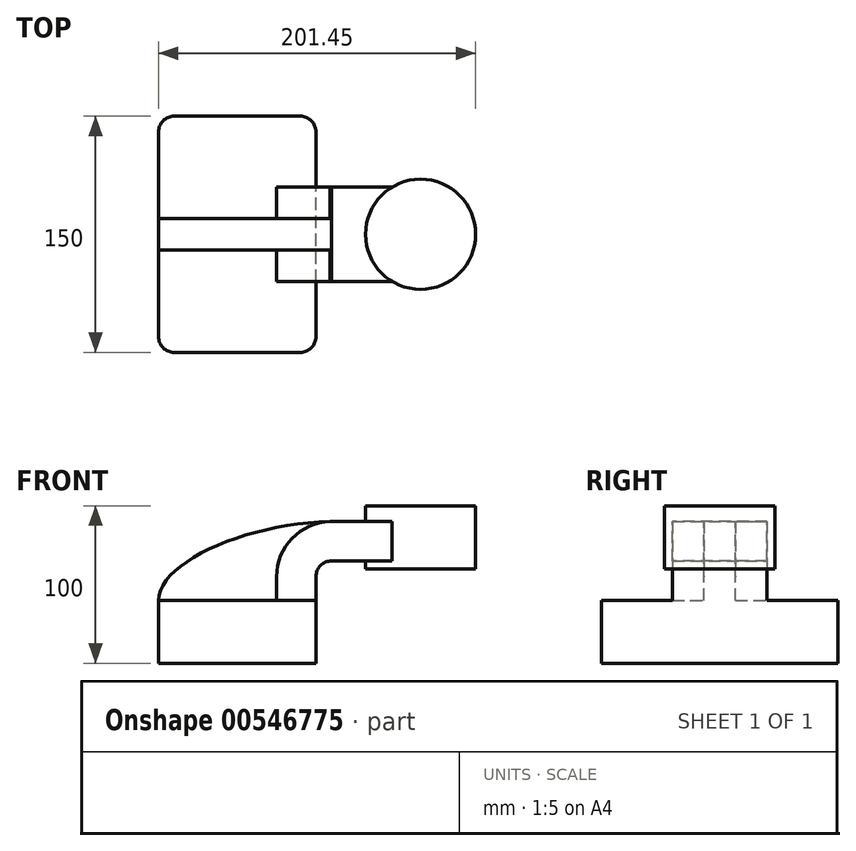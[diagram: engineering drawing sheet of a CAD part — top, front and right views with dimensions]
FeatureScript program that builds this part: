
annotation { "Feature Type Name" : "Feature", "Feature Type Description" : "" }
export const myFeature = defineFeature(function(context is Context, id is Id, definition is map)
    precondition{}
    {
        {
            var Q0;
            Q0=qCreatedBy(makeId("Front.planeOp"),FACE);
            var sketch = newSketch(context, id + "F0", { "sketchPlane" : qUnion([Q0])});
            skLineSegment(sketch, "E0.bottom", {"start": v(50, -20) * mm, "end": v(-50, -20) * mm});
            skLineSegment(sketch, "E0.top", {"start": v(50, 20) * mm, "end": v(-50, 20) * mm});
            skLineSegment(sketch, "E0.left", {"start": v(50, -20) * mm, "end": v(50, 20) * mm});
            skLineSegment(sketch, "E0.right", {"start": v(-50, -20) * mm, "end": v(-50, 20) * mm});
            skPoint(sketch, "E0.middle", {"position": v(0, 0) * mm});
            skLineSegment(sketch, "E1.bottom", {"start": v(151.45, 40) * mm, "end": v(81.45, 40) * mm});
            skLineSegment(sketch, "E1.top", {"start": v(151.45, 80) * mm, "end": v(81.45, 80) * mm});
            skLineSegment(sketch, "E1.left", {"start": v(151.45, 40) * mm, "end": v(151.45, 80) * mm});
            skLineSegment(sketch, "E1.right", {"start": v(81.45, 40) * mm, "end": v(81.45, 80) * mm});
            skPoint(sketch, "E1.middle", {"position": v(116.45, 60) * mm});
            skLineSegment(sketch, "E2", {"start": v(116.45, 80) * mm, "end": v(116.45, 40) * mm});
            skLineSegment(sketch, "E3", {"start": v(50, 20) * mm, "end": v(50, 35) * mm});
            skArc(sketch, "E4", {"start": v(50, 35) * mm, "mid": v(52.93, 42.07) * mm, "end": v(60, 45) * mm});
            skLineSegment(sketch, "E5", {"start": v(60, 45) * mm, "end": v(116.45, 45) * mm});
            skLineSegment(sketch, "E6.0", {"start": v(60, 70) * mm, "end": v(116.45, 70) * mm});
            skArc(sketch, "E6.1", {"start": v(25, 35) * mm, "mid": v(35.25, 59.75) * mm, "end": v(60, 70) * mm});
            skLineSegment(sketch, "E6.2", {"start": v(25, 20) * mm, "end": v(25, 35) * mm});
            skFitSpline(sketch, "E7", {"points": [v(-50, 20) * mm, v(60, 70) * mm], "startDerivative": vector(0.62, 73.71) * mm, "endDerivative": vector(158.33, 1.96) * mm});
            skSolve(sketch);
        }
        {
            var Q0;
            Q0=makeQuery(id+"F0.imprint","IMPRINT",FACE,{"disambiguationData":[TD([[makeQuery(id+"F0.imprint","IMPRINT",EDGE,{"derivedFrom":sQuery(id+"F0.wireOp",EDGE,"E0.bottom")}),-1.0]])]});
            extrude(context, id + "F1", {"entities" : qUnion([Q0]), "endBound" : BoundingType.SYMMETRIC, "depth" : 150 * mm, "offsetDistance" : 25 * mm});
        }
        {
            var Q0;
            {var subQ1=sQuery(id+"F0.wireOp",EDGE,"E3");Q0=makeQuery(id+"F0.imprint","IMPRINT",FACE,{"disambiguationData":[TD([[makeQuery(id+"F0.imprint","IMPRINT",EDGE,{"derivedFrom":subQ1}),1.0]])]});}
            var Q1;
            {var subQ0=sQuery(id+"F0.wireOp",EDGE,"E5");var subQ1=sQuery(id+"F0.wireOp",EDGE,"E1.right");var subQ2=makeQuery(id+"F0.imprint","INTERSECT",VERTEX,{"derivedFrom":[subQ1,subQ0]});Q1=makeQuery(id+"F0.imprint","IMPRINT",FACE,{"disambiguationData":[TD([[makeQuery(id+"F0.imprint","IMPRINT",EDGE,{"disambiguationData":[TD([[subQ2,-1.0]])],"derivedFrom":subQ1}),-1.0]])]});}
            extrude(context, id + "F2", {"entities" : qUnion([Q0, Q1]), "operationType" : NewBodyOperationType.ADD, "endBound" : BoundingType.SYMMETRIC, "depth" : 60 * mm, "offsetDistance" : 25 * mm});
        }
        {
            var Q0;
            {var subQ3=sQuery(id+"F0.wireOp",EDGE,"E6.2");Q0=makeQuery(id+"F0.imprint","IMPRINT",FACE,{"disambiguationData":[TD([[makeQuery(id+"F0.imprint","IMPRINT",EDGE,{"derivedFrom":subQ3}),1.0]])]});}
            extrude(context, id + "F3", {"entities" : qUnion([Q0]), "operationType" : NewBodyOperationType.ADD, "endBound" : BoundingType.SYMMETRIC, "depth" : 20 * mm, "offsetDistance" : 25 * mm});
        }
        {
            var Q0;
            {var subQ4=sQuery(id+"F0.wireOp",EDGE,"E1.left");Q0=makeQuery(id+"F0.imprint","IMPRINT",FACE,{"disambiguationData":[TD([[makeQuery(id+"F0.imprint","IMPRINT",EDGE,{"derivedFrom":subQ4}),1.0]])]});}
            var Q1;
            Q1=sQuery(id+"F0.wireOp",EDGE,"E2");
            revolve(context, id + "F4", {"operationType" : NewBodyOperationType.ADD, "entities" : qUnion([Q0]), "axis" : qUnion([Q1]), "revolveType" : RevolveType.FULL});
        }
        {
            var Q0;
            Q0=makeQuery(id+"F1.opExtrude","CAP_EDGE",EDGE,{"disambiguationData":[OSD([sQuery(id+"F0.wireOp",EDGE,"E0.left")])],"isStart":false});
            var Q1;
            Q1=makeQuery(id+"F1.opExtrude","CAP_EDGE",EDGE,{"disambiguationData":[OSD([sQuery(id+"F0.wireOp",EDGE,"E0.right")])],"isStart":false});
            var Q2;
            Q2=makeQuery(id+"F1.opExtrude","CAP_EDGE",EDGE,{"disambiguationData":[OSD([sQuery(id+"F0.wireOp",EDGE,"E0.right")])],"isStart":true});
            var Q3;
            Q3=makeQuery(id+"F1.opExtrude","CAP_EDGE",EDGE,{"disambiguationData":[OSD([sQuery(id+"F0.wireOp",EDGE,"E0.left")])],"isStart":true});
            fillet(context, id + "F5", {"entities" : qUnion([Q0, Q1, Q2, Q3]), "radius" : 10 * mm, "tangentPropagation" : true, "allowEdgeOverflow" : false});
        }
    });
